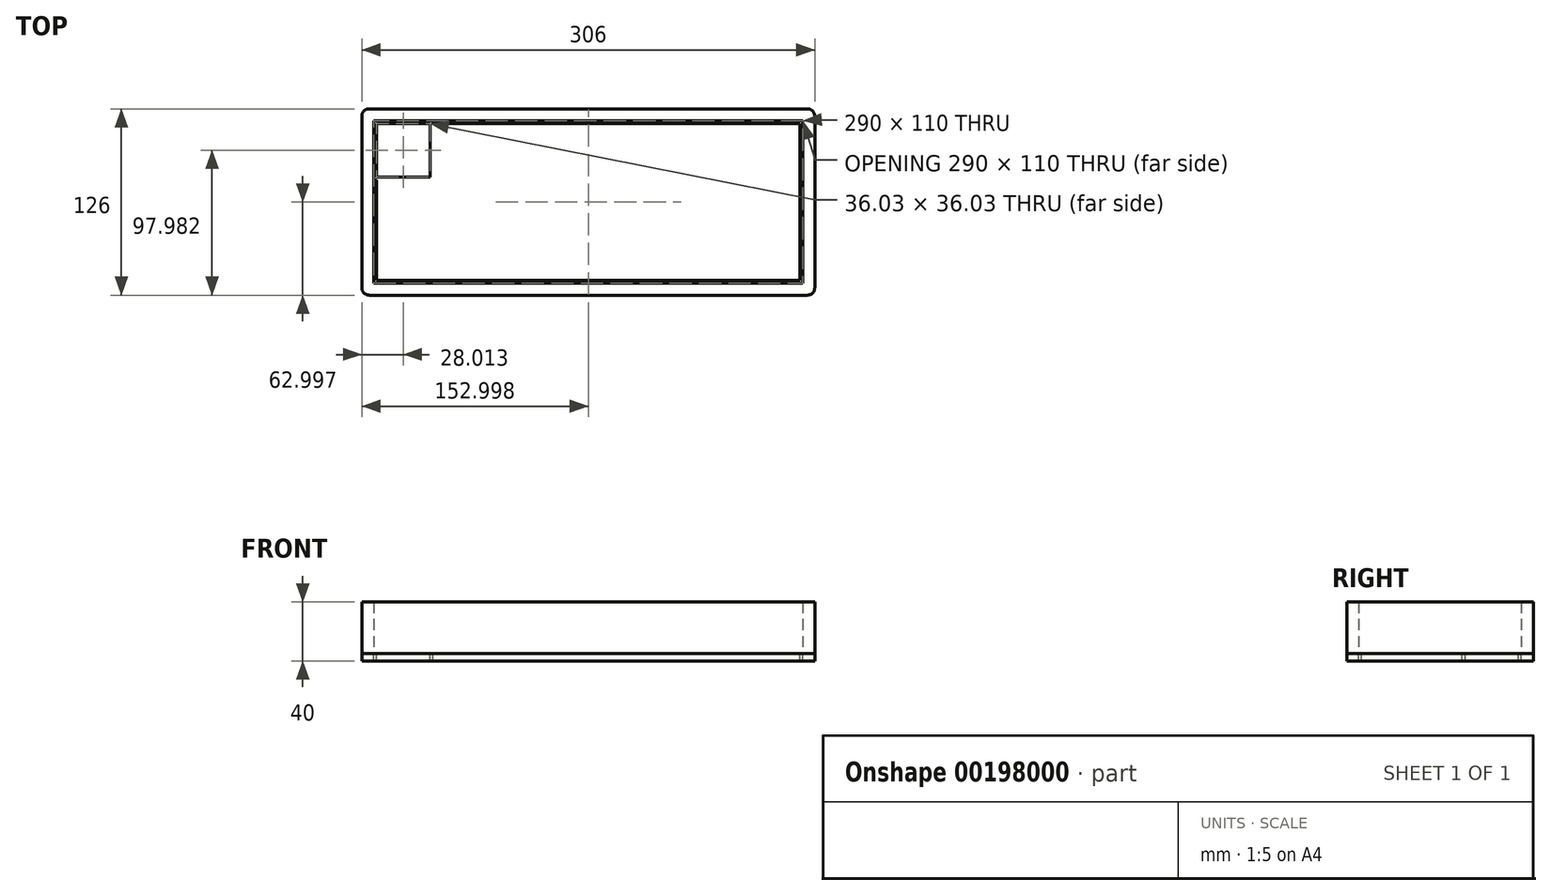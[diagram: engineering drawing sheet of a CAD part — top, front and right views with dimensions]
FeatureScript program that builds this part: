
annotation { "Feature Type Name" : "Feature", "Feature Type Description" : "" }
export const myFeature = defineFeature(function(context is Context, id is Id, definition is map)
    precondition{}
    {
        {
            var Q0;
            Q0=qCreatedBy(makeId("Top.planeOp"),FACE);
            var sketch = newSketch(context, id + "F0", { "sketchPlane" : qUnion([Q0])});
            skLineSegment(sketch, "E0.bottom", {"start": v(156.65, 53.77) * mm, "end": v(-133.35, 53.77) * mm});
            skLineSegment(sketch, "E0.top", {"start": v(156.65, -56.23) * mm, "end": v(-133.35, -56.23) * mm});
            skLineSegment(sketch, "E0.left", {"start": v(156.65, 53.77) * mm, "end": v(156.65, -56.23) * mm});
            skLineSegment(sketch, "E0.right", {"start": v(-133.35, 53.77) * mm, "end": v(-133.35, -56.23) * mm});
            skLineSegment(sketch, "E1.0", {"start": v(159.65, 61.77) * mm, "end": v(-136.35, 61.77) * mm});
            skLineSegment(sketch, "E1.1", {"start": v(164.65, 56.77) * mm, "end": v(164.65, -59.23) * mm});
            skLineSegment(sketch, "E1.2", {"start": v(159.65, -64.23) * mm, "end": v(-136.35, -64.23) * mm});
            skLineSegment(sketch, "E1.3", {"start": v(-141.35, 56.77) * mm, "end": v(-141.35, -59.23) * mm});
            skPoint(sketch, "E2.visualSharp", {"position": v(164.65, 61.77) * mm});
            skArc(sketch, "E2.filletArc", {"start": v(164.65, 56.77) * mm, "mid": v(163.18, 60.3) * mm, "end": v(159.65, 61.77) * mm});
            skPoint(sketch, "E3.visualSharp", {"position": v(-141.35, 61.77) * mm});
            skArc(sketch, "E3.filletArc", {"start": v(-136.35, 61.77) * mm, "mid": v(-139.89, 60.3) * mm, "end": v(-141.35, 56.77) * mm});
            skPoint(sketch, "E4.visualSharp", {"position": v(-141.35, -64.23) * mm});
            skArc(sketch, "E4.filletArc", {"start": v(-141.35, -59.23) * mm, "mid": v(-139.89, -62.77) * mm, "end": v(-136.35, -64.23) * mm});
            skPoint(sketch, "E5.visualSharp", {"position": v(164.65, -64.23) * mm});
            skArc(sketch, "E5.filletArc", {"start": v(159.65, -64.23) * mm, "mid": v(163.18, -62.77) * mm, "end": v(164.65, -59.23) * mm});
            skLineSegment(sketch, "E6.0", {"start": v(154.65, 51.77) * mm, "end": v(-131.35, 51.77) * mm});
            skLineSegment(sketch, "E6.1", {"start": v(154.65, 51.77) * mm, "end": v(154.65, -54.23) * mm});
            skLineSegment(sketch, "E6.2", {"start": v(154.65, -54.23) * mm, "end": v(-131.35, -54.23) * mm});
            skLineSegment(sketch, "E6.3", {"start": v(-131.35, 51.77) * mm, "end": v(-131.35, -54.23) * mm});
            skLineSegment(sketch, "E7.bottom", {"start": v(-131.35, 51.77) * mm, "end": v(-95.32, 51.77) * mm});
            skLineSegment(sketch, "E7.top", {"start": v(-131.35, 15.74) * mm, "end": v(-95.32, 15.74) * mm});
            skLineSegment(sketch, "E7.left", {"start": v(-131.35, 51.77) * mm, "end": v(-131.35, 15.74) * mm});
            skLineSegment(sketch, "E7.right", {"start": v(-95.32, 51.77) * mm, "end": v(-95.32, 15.74) * mm});
            skLineSegment(sketch, "E8.0", {"start": v(-93.32, 53.77) * mm, "end": v(-93.32, 13.74) * mm});
            skLineSegment(sketch, "E8.1", {"start": v(-133.35, 53.77) * mm, "end": v(-93.32, 53.77) * mm});
            skLineSegment(sketch, "E8.2", {"start": v(-133.35, 53.77) * mm, "end": v(-133.35, 13.74) * mm});
            skLineSegment(sketch, "E8.3", {"start": v(-133.35, 13.74) * mm, "end": v(-93.32, 13.74) * mm});
            skPoint(sketch, "E9.oppositeSnap0", {"position": v(-93.32, 33.75) * mm});
            skLineSegment(sketch, "E9.bottom", {"start": v(-95.32, 33.75) * mm, "end": v(-90.3, 33.75) * mm});
            skLineSegment(sketch, "E9.top", {"start": v(-95.32, 33.75) * mm, "end": v(-90.3, 33.75) * mm});
            skLineSegment(sketch, "E9.left", {"start": v(-95.32, 33.75) * mm, "end": v(-95.32, 33.75) * mm});
            skLineSegment(sketch, "E9.right", {"start": v(-90.3, 33.75) * mm, "end": v(-90.3, 33.75) * mm});
            skSolve(sketch);
        }
        {
            var Q0;
            Q0=makeQuery(id+"F0.imprint","IMPRINT",FACE,{"disambiguationData":[TD([[makeQuery(id+"F0.imprint","IMPRINT",EDGE,{"derivedFrom":sQuery(id+"F0.wireOp",EDGE,"E0.bottom")}),-1.0]])]});
            var Q1;
            {var subQ2=sQuery(id+"F0.wireOp",EDGE,"E7.bottom");Q1=makeQuery(id+"F0.imprint","IMPRINT",FACE,{"disambiguationData":[TD([[makeQuery(id+"F0.imprint","IMPRINT",EDGE,{"derivedFrom":subQ2}),1.0]])]});}
            var Q2;
            {var subQ6=sQuery(id+"F0.wireOp",EDGE,"E7.top");Q2=makeQuery(id+"F0.imprint","IMPRINT",FACE,{"disambiguationData":[TD([[makeQuery(id+"F0.imprint","IMPRINT",EDGE,{"derivedFrom":subQ6}),-1.0]])]});}
            var Q3;
            {var subQ3=sQuery(id+"F0.wireOp",EDGE,"E8.0");var subQ5=sQuery(id+"F0.wireOp",EDGE,"E9.top");var subQ7=makeQuery(id+"F0.imprint","INTERSECT",VERTEX,{"derivedFrom":[subQ3,subQ5]});Q3=makeQuery(id+"F0.imprint","IMPRINT",FACE,{"disambiguationData":[TD([[makeQuery(id+"F0.imprint","IMPRINT",EDGE,{"disambiguationData":[TD([[subQ7,1.0]])],"derivedFrom":subQ3}),-1.0]])]});}
            var Q4;
            {var subQ1=sQuery(id+"F0.wireOp",EDGE,"E7.bottom");Q4=makeQuery(id+"F0.imprint","IMPRINT",FACE,{"disambiguationData":[TD([[makeQuery(id+"F0.imprint","IMPRINT",EDGE,{"derivedFrom":subQ1}),-1.0]])]});}
            var Q5;
            {var subQ8=sQuery(id+"F0.wireOp",EDGE,"E6.1");Q5=makeQuery(id+"F0.imprint","IMPRINT",FACE,{"disambiguationData":[TD([[makeQuery(id+"F0.imprint","IMPRINT",EDGE,{"derivedFrom":subQ8}),-1.0]])]});}
            var Q6;
            {var subQ2=sQuery(id+"F0.wireOp",EDGE,"E0.bottom");Q6=makeQuery(id+"F0.imprint","IMPRINT",FACE,{"disambiguationData":[TD([[makeQuery(id+"F0.imprint","IMPRINT",EDGE,{"derivedFrom":subQ2}),1.0]])]});}
            extrude(context, id + "F1", {"entities" : qUnion([Q0, Q1, Q2, Q3, Q4, Q5, Q6]), "oppositeDirection" : true, "depth" : 5 * mm});
        }
        {
            var Q0;
            Q0=makeQuery(id+"F0.imprint","IMPRINT",FACE,{"disambiguationData":[TD([[makeQuery(id+"F0.imprint","IMPRINT",EDGE,{"derivedFrom":sQuery(id+"F0.wireOp",EDGE,"E0.bottom")}),-1.0]])]});
            extrude(context, id + "F2", {"entities" : qUnion([Q0]), "depth" : 35 * mm});
        }
    });
